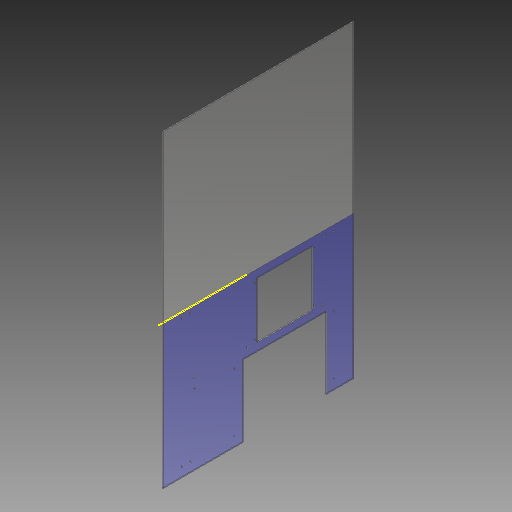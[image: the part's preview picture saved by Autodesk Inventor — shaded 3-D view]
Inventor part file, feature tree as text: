
AUTODESK INVENTOR PART (.ipt)
format: ipt  version: 2018 (Build 220112000, 112)  size: 133,632 bytes
history: native  units: in
note: dims shown in document units (in); Inventor stores cm internally (conversion verified against a paired STEP export)
features: plane x1, split x1, other x1
ambient origin geometry x8: Origin, YZ Plane, XZ Plane, XY Plane, X Axis, Y Axis, Z Axis, Center Point
bodies: Solid1 (feature_tree)
feature tree (3):
  plane  "Work Plane1"
  split  "Split1"
  other  "1_4 (0.25) Diameter Hole1"
